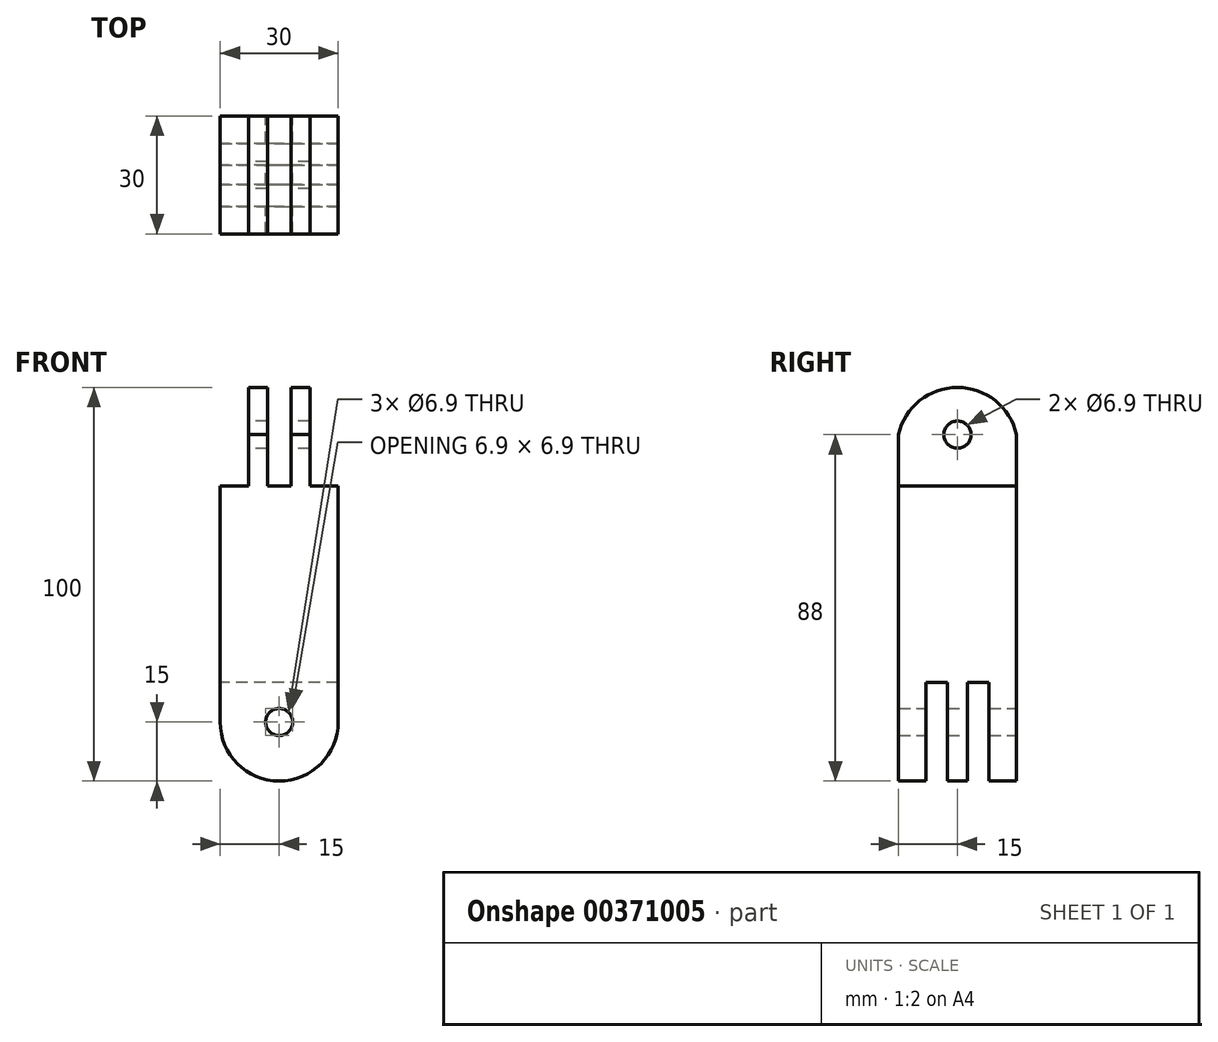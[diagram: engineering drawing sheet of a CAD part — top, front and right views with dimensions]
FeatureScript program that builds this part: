
annotation { "Feature Type Name" : "Feature", "Feature Type Description" : "" }
export const myFeature = defineFeature(function(context is Context, id is Id, definition is map)
    precondition{}
    {
        {
            var Q0;
            Q0=qCreatedBy(makeId("Right.planeOp"),FACE);
            var sketch = newSketch(context, id + "F0", { "sketchPlane" : qUnion([Q0])});
            skLineSegment(sketch, "E0.bottom", {"start": v(15, 37.5) * mm, "end": v(-15, 37.5) * mm});
            skLineSegment(sketch, "E0.top", {"start": v(15, -37.5) * mm, "end": v(-15, -37.5) * mm});
            skLineSegment(sketch, "E0.left", {"start": v(15, 37.5) * mm, "end": v(15, -37.5) * mm});
            skLineSegment(sketch, "E0.right", {"start": v(-15, 37.5) * mm, "end": v(-15, -37.5) * mm});
            skPoint(sketch, "E0.middle", {"position": v(0, 0) * mm});
            skSolve(sketch);
        }
        {
            var Q0;
            Q0 = qSketchRegion(id + "F0", true);
            extrude(context, id + "F1", {"entities" : qUnion([Q0]), "depth" : 30 * mm});
        }
        {
            var Q0;
            Q0=makeQuery(id+"F1.opExtrude","SWEPT_FACE",FACE,{"disambiguationData":[OSD([sQuery(id+"F0.wireOp",EDGE,"E0.top")])]});
            var sketch = newSketch(context, id + "F2", { "sketchPlane" : qUnion([Q0])});
            skLineSegment(sketch, "E1.bottom", {"start": v(30, 8) * mm, "end": v(0, 8) * mm});
            skLineSegment(sketch, "E1.top", {"start": v(30, 2.5) * mm, "end": v(0, 2.5) * mm});
            skLineSegment(sketch, "E1.left", {"start": v(30, 8) * mm, "end": v(30, 2.5) * mm});
            skLineSegment(sketch, "E1.right", {"start": v(0, 8) * mm, "end": v(0, 2.5) * mm});
            skLineSegment(sketch, "E2.bottom", {"start": v(30, -2.5) * mm, "end": v(0, -2.5) * mm});
            skLineSegment(sketch, "E2.top", {"start": v(30, -8) * mm, "end": v(0, -8) * mm});
            skLineSegment(sketch, "E2.left", {"start": v(30, -2.5) * mm, "end": v(30, -8) * mm});
            skLineSegment(sketch, "E2.right", {"start": v(0, -2.5) * mm, "end": v(0, -8) * mm});
            skSolve(sketch);
        }
        {
            var Q0;
            Q0=makeQuery(id+"F1.opExtrude","SWEPT_FACE",FACE,{"disambiguationData":[OSD([sQuery(id+"F0.wireOp",EDGE,"E0.left")])]});
            var sketch = newSketch(context, id + "F3", { "sketchPlane" : qUnion([Q0])});
            skPoint(sketch, "E3", {"position": v(-15, -37.5) * mm});
            skPoint(sketch, "E4", {"position": v(-30, -22.5) * mm});
            skPoint(sketch, "E5", {"position": v(0, -22.5) * mm});
            skArc(sketch, "E6", {"start": v(-30, -22.5) * mm, "mid": v(-15, -37.5) * mm, "end": v(0, -22.5) * mm});
            skCircle(sketch, "E7", {"center": v(-15, -22.5) * mm, "radius": 3.45 * mm});
            skSolve(sketch);
        }
        {
            var Q0;
            {var subQ0=sQuery(id+"F3.wireOp",EDGE,"E6");var subQ1=sQuery(id+"F0.wireOp",EDGE,"E0.left");var subQ2=makeQuery(id+"F1.opExtrude","CAP_EDGE",EDGE,{"disambiguationData":[OSD([subQ1])],"isStart":false});var subQ3=makeQuery(id+"F3.imprint","INTERSECT",VERTEX,{"disambiguationData":[OD(1.0)],"derivedFrom":[subQ2,subQ0]});Q0=makeQuery(id+"F3.imprint","IMPRINT",FACE,{"disambiguationData":[TD([[makeQuery(id+"F3.imprint","IMPRINT",EDGE,{"disambiguationData":[TD([[subQ3,-1.0]])],"derivedFrom":subQ0}),-1.0]])]});}
            var Q1;
            {var subQ0=sQuery(id+"F3.wireOp",EDGE,"E6");var subQ1=sQuery(id+"F0.wireOp",EDGE,"E0.left");var subQ4=makeQuery(id+"F1.opExtrude","CAP_EDGE",EDGE,{"disambiguationData":[OSD([subQ1])],"isStart":true});var subQ5=makeQuery(id+"F3.imprint","INTERSECT",VERTEX,{"disambiguationData":[OD(1.0)],"derivedFrom":[subQ4,subQ0]});Q1=makeQuery(id+"F3.imprint","IMPRINT",FACE,{"disambiguationData":[TD([[makeQuery(id+"F3.imprint","IMPRINT",EDGE,{"disambiguationData":[TD([[subQ5,1.0]])],"derivedFrom":subQ0}),-1.0]])]});}
            extrude(context, id + "F4", {"entities" : qUnion([Q0, Q1]), "operationType" : NewBodyOperationType.REMOVE, "endBound" : BoundingType.THROUGH_ALL, "oppositeDirection" : true, "depth" : 25 * mm});
        }
        {
            var Q0;
            Q0=makeQuery(id+"F2.imprint","IMPRINT",FACE,{"disambiguationData":[TD([[makeQuery(id+"F2.imprint","IMPRINT",EDGE,{"derivedFrom":sQuery(id+"F2.wireOp",EDGE,"E1.bottom")}),1.0]])]});
            var Q1;
            Q1=makeQuery(id+"F2.imprint","IMPRINT",FACE,{"disambiguationData":[TD([[makeQuery(id+"F2.imprint","IMPRINT",EDGE,{"derivedFrom":sQuery(id+"F2.wireOp",EDGE,"E2.bottom")}),1.0]])]});
            extrude(context, id + "F5", {"entities" : qUnion([Q0, Q1]), "operationType" : NewBodyOperationType.REMOVE, "oppositeDirection" : true, "depth" : 25 * mm});
        }
        {
            var Q0;
            Q0 = qSketchRegion(id + "F3", true);
            extrude(context, id + "F6", {"entities" : qUnion([Q0]), "operationType" : NewBodyOperationType.REMOVE, "endBound" : BoundingType.THROUGH_ALL, "oppositeDirection" : true, "depth" : 25 * mm});
        }
        {
            var Q0;
            Q0=makeQuery(id+"F1.opExtrude","SWEPT_FACE",FACE,{"disambiguationData":[OSD([sQuery(id+"F0.wireOp",EDGE,"E0.bottom")])]});
            var sketch = newSketch(context, id + "F7", { "sketchPlane" : qUnion([Q0])});
            skLineSegment(sketch, "E8.bottom", {"start": v(7.2, 15) * mm, "end": v(12, 15) * mm});
            skLineSegment(sketch, "E8.top", {"start": v(7.2, -15) * mm, "end": v(12, -15) * mm});
            skLineSegment(sketch, "E8.left", {"start": v(7.2, 15) * mm, "end": v(7.2, -15) * mm});
            skLineSegment(sketch, "E8.right", {"start": v(12, 15) * mm, "end": v(12, -15) * mm});
            skLineSegment(sketch, "E9.bottom", {"start": v(18, 15) * mm, "end": v(22.8, 15) * mm});
            skLineSegment(sketch, "E9.top", {"start": v(18, -15) * mm, "end": v(22.8, -15) * mm});
            skLineSegment(sketch, "E9.left", {"start": v(18, 15) * mm, "end": v(18, -15) * mm});
            skLineSegment(sketch, "E9.right", {"start": v(22.8, 15) * mm, "end": v(22.8, -15) * mm});
            skSolve(sketch);
        }
        {
            var Q0;
            Q0 = qSketchRegion(id + "F7", true);
            extrude(context, id + "F8", {"entities" : qUnion([Q0]), "operationType" : NewBodyOperationType.ADD, "depth" : 25 * mm});
        }
        {
            var Q0;
            Q0=makeQuery(id+"F8.opExtrude","SWEPT_FACE",FACE,{"disambiguationData":[OSD([sQuery(id+"F7.wireOp",EDGE,"E8.left")])]});
            var sketch = newSketch(context, id + "F9", { "sketchPlane" : qUnion([Q0])});
            skPoint(sketch, "E10", {"position": v(0, 62.5) * mm});
            skPoint(sketch, "E11", {"position": v(15, 50.5) * mm});
            skPoint(sketch, "E12", {"position": v(-15, 50.5) * mm});
            skArc(sketch, "E13", {"start": v(15, 50.5) * mm, "mid": v(0, 62.5) * mm, "end": v(-15, 50.5) * mm});
            skPoint(sketch, "E14", {"position": v(0, 50.5) * mm});
            skCircle(sketch, "E15", {"center": v(0, 50.5) * mm, "radius": 3.45 * mm});
            skSolve(sketch);
        }
        {
            var Q0;
            {var subQ0=sQuery(id+"F9.wireOp",EDGE,"E13");var subQ1=sQuery(id+"F7.wireOp",EDGE,"E8.left");var subQ4=makeQuery(id+"F8.opExtrude","CAP_EDGE",EDGE,{"disambiguationData":[OSD([subQ1])],"isStart":false});var subQ5=makeQuery(id+"F9.imprint","INTERSECT",VERTEX,{"derivedFrom":[subQ4,subQ0]});Q0=makeQuery(id+"F9.imprint","IMPRINT",FACE,{"disambiguationData":[TD([[makeQuery(id+"F9.imprint","IMPRINT",EDGE,{"disambiguationData":[TD([[subQ5,-1.0]])],"derivedFrom":subQ0}),-1.0]])]});}
            var Q1;
            {var subQ0=sQuery(id+"F9.wireOp",EDGE,"E13");var subQ1=sQuery(id+"F7.wireOp",EDGE,"E8.left");var subQ4=makeQuery(id+"F8.opExtrude","CAP_EDGE",EDGE,{"disambiguationData":[OSD([subQ1])],"isStart":false});var subQ5=makeQuery(id+"F9.imprint","INTERSECT",VERTEX,{"derivedFrom":[subQ4,subQ0]});Q1=makeQuery(id+"F9.imprint","IMPRINT",FACE,{"disambiguationData":[TD([[makeQuery(id+"F9.imprint","IMPRINT",EDGE,{"disambiguationData":[TD([[subQ5,1.0]])],"derivedFrom":subQ0}),-1.0]])]});}
            extrude(context, id + "F10", {"entities" : qUnion([Q0, Q1]), "operationType" : NewBodyOperationType.REMOVE, "endBound" : BoundingType.THROUGH_ALL, "oppositeDirection" : true, "depth" : 25 * mm});
        }
        {
            var Q0;
            Q0 = qSketchRegion(id + "F9", true);
            extrude(context, id + "F11", {"entities" : qUnion([Q0]), "operationType" : NewBodyOperationType.REMOVE, "endBound" : BoundingType.THROUGH_ALL, "oppositeDirection" : true, "depth" : 25 * mm});
        }
    });
